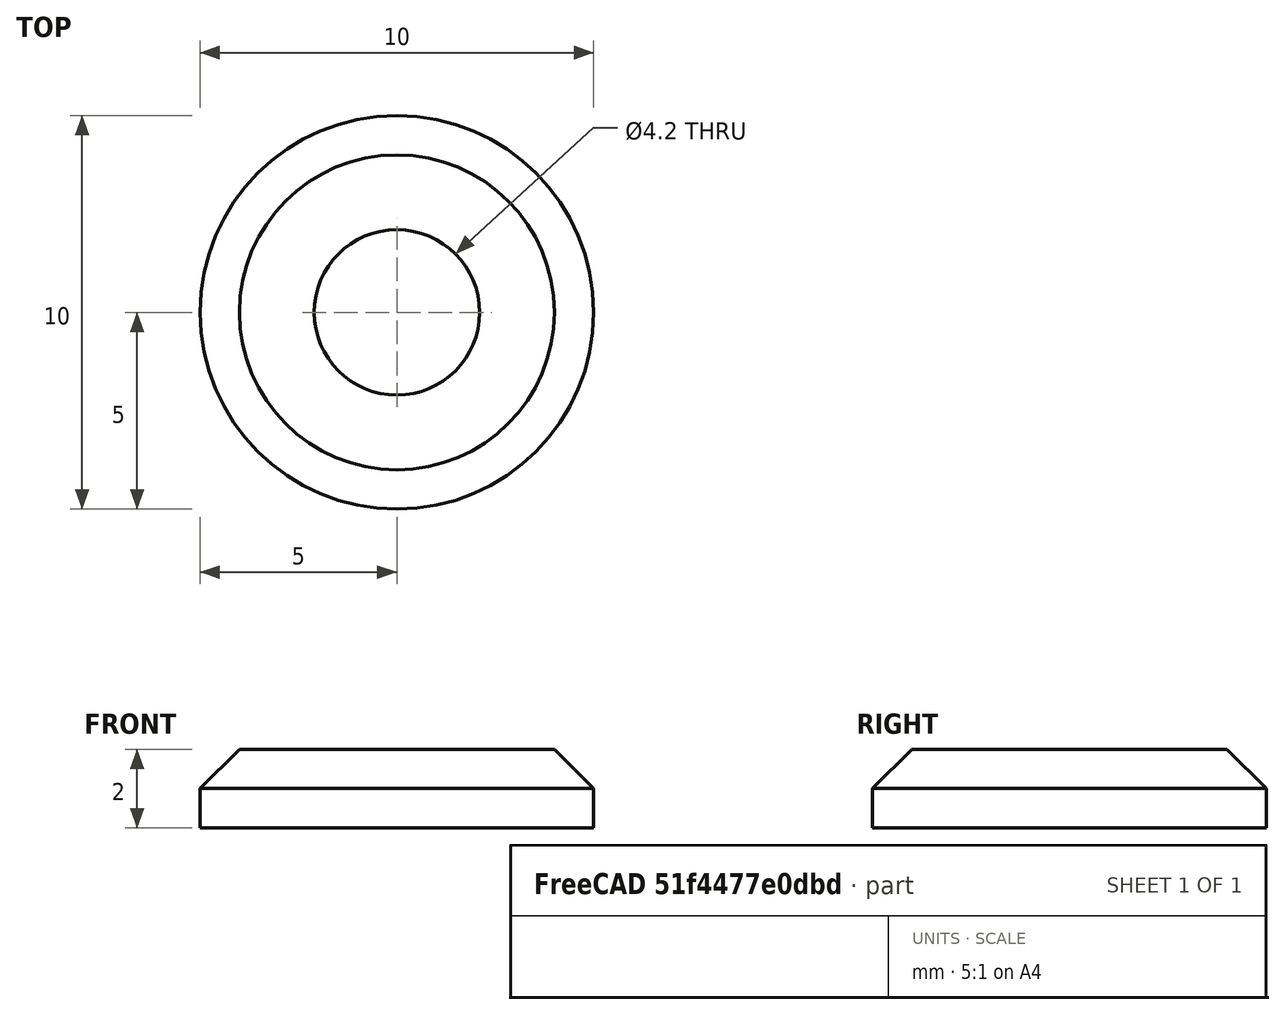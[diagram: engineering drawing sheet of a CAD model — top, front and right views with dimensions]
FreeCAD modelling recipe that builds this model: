
FCSTD DOCUMENT  (FreeCAD 0.20R29410 (Git))
Label: Washer Printed
License: All rights reserved
LicenseURL: http://en.wikipedia.org/wiki/All_rights_reserved
objects: Sketcher::SketchObject×1, PartDesign::Revolution×1, PartDesign::Body×1, Spreadsheet::Sheet×1
note: 4 computed .brp shape members not serialized (recipe doc carries the construction recipe); baked Part::Feature solids carry a one-line shape summary decoded from their .brp
EXTERNAL_REF file=Tailbox.FCStd obj=Spreadsheet

FEATURE [Sketcher::SketchObject] Sketch
  FullyConstrained = true
  MapMode = 5
  Placement = pos=(0,0,0) rot=(1,0,0;1.5708rad)
  Support = -> [XZ_Plane]
  expr: Constraints[8] = Tailbox#<<dims>>.bolt_d / 2
  sketch-geometry (5):
    g0: LineSegment StartX=2.1 StartY=0 StartZ=0 EndX=2.1 EndY=2 EndZ=0
    g1: LineSegment StartX=2.1 StartY=2 StartZ=0 EndX=4 EndY=2 EndZ=0
    g2: LineSegment StartX=4 StartY=2 StartZ=0 EndX=5 EndY=1 EndZ=0
    g3: LineSegment StartX=5 StartY=1 StartZ=0 EndX=5 EndY=0 EndZ=0
    g4: LineSegment StartX=5 StartY=0 StartZ=0 EndX=2.1 EndY=0 EndZ=0
  constraints (15):
    c: Coincident(g0,g1)
    c: Horizontal(g1)
    c: Coincident(g1,g2)
    c: Coincident(g2,g3)
    c: Vertical(g3)
    c: Coincident(g3,g4)
    c: Coincident(g4,g0)
    c: Horizontal(g4)
    c: DistanceX(g0) = 2.1
    c: PointOnObject(g0,g-1)
    c: Vertical(g0)
    c: DistanceX(g3) = 5
    c: DistanceY(g0,g0) = 2
    c: Angle(g2,g4) = 0.785398
    c: DistanceX(g1) = 4
FEATURE [PartDesign::Revolution] Revolution
  Angle = 360
  Axis = (0,2e-16,1)
  Base = (0,0,0)
  Placement = pos=(0,0,0) rot=(1,0,0;1.5708rad)
  Profile = -> Sketch
  ReferenceAxis = -> Sketch [V_Axis]
  Reversed = true
FEATURE [PartDesign::Body] Body
  Group = -> [Sketch,Revolution]
  Origin = -> Origin
  Tip = -> Revolution
FEATURE [Spreadsheet::Sheet] _PARTINFO_  label="#PARTINFO#"
  cells = A1=IDENTNO; A2=DESCRIPTION; B2=Washer Printed; A3=SUPPLIER; A4=SUPP.IDENTNO; A5=SUPP.DESCRIPTION; A6=(FILENAME)
